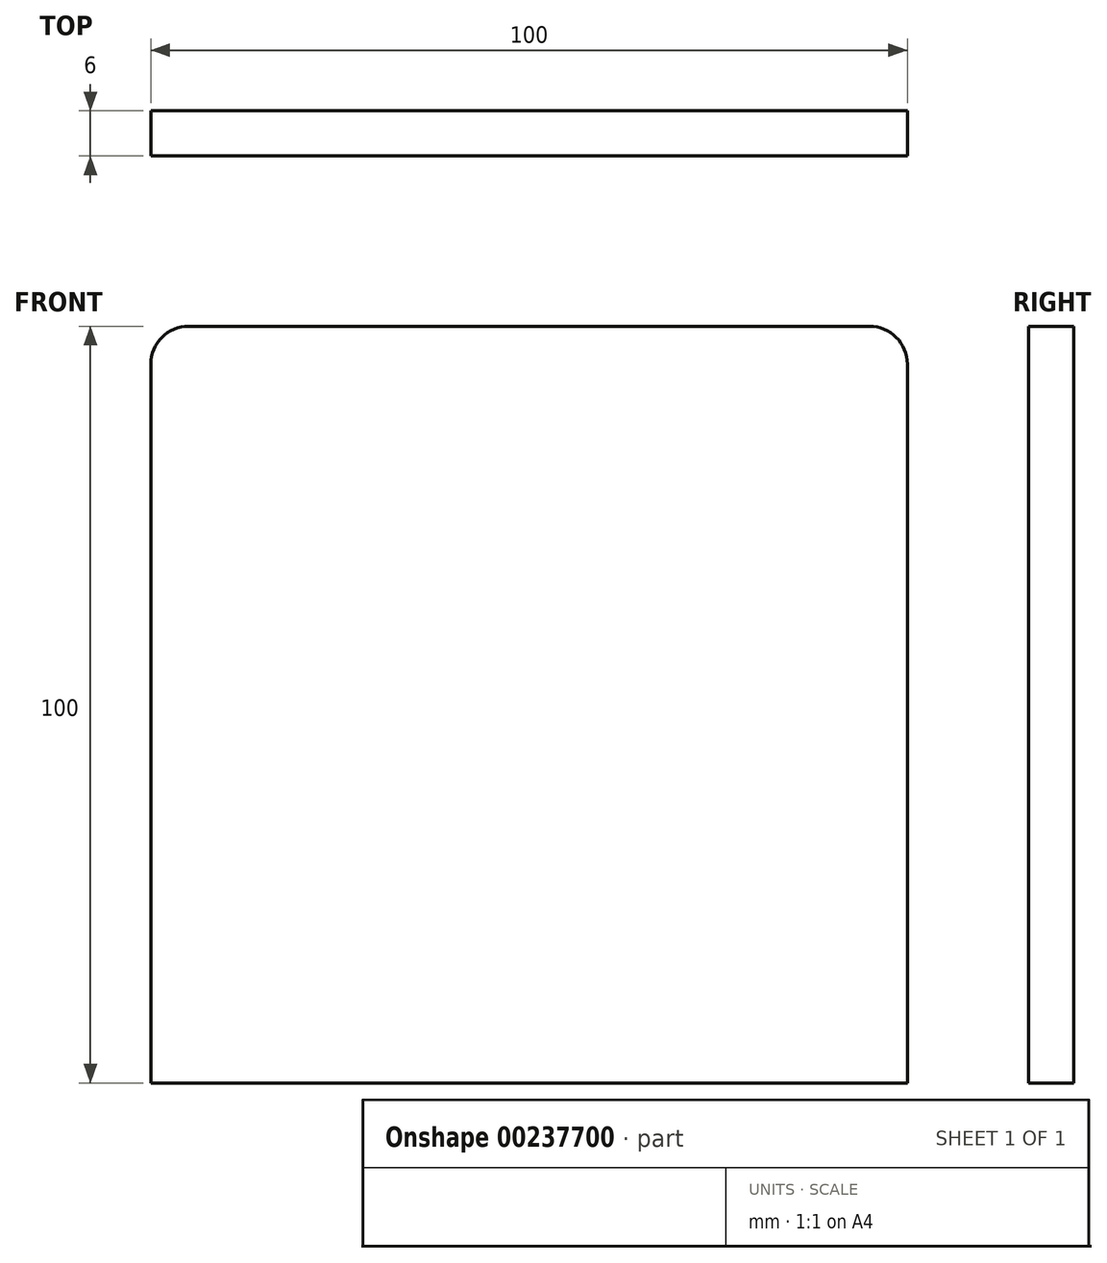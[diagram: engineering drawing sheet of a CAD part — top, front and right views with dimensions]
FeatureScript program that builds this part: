
annotation { "Feature Type Name" : "Feature", "Feature Type Description" : "" }
export const myFeature = defineFeature(function(context is Context, id is Id, definition is map)
    precondition{}
    {
        {
            var Q0;
            Q0=qCreatedBy(makeId("Front.planeOp"),FACE);
            var sketch = newSketch(context, id + "F0", { "sketchPlane" : qUnion([Q0])});
            skLineSegment(sketch, "E0.bottom", {"start": v(45, 50) * mm, "end": v(-45, 50) * mm});
            skLineSegment(sketch, "E0.top", {"start": v(50, -50) * mm, "end": v(-50, -50) * mm});
            skLineSegment(sketch, "E0.left", {"start": v(50, 45) * mm, "end": v(50, -50) * mm});
            skLineSegment(sketch, "E0.right", {"start": v(-50, 45) * mm, "end": v(-50, -50) * mm});
            skPoint(sketch, "E0.middle", {"position": v(0, 0) * mm});
            skPoint(sketch, "E1.visualSharp", {"position": v(-50, 50) * mm});
            skArc(sketch, "E1.filletArc", {"start": v(-45, 50) * mm, "mid": v(-48.54, 48.54) * mm, "end": v(-50, 45) * mm});
            skPoint(sketch, "E2.visualSharp", {"position": v(50, 50) * mm});
            skArc(sketch, "E2.filletArc", {"start": v(50, 45) * mm, "mid": v(48.54, 48.54) * mm, "end": v(45, 50) * mm});
            skLineSegment(sketch, "E3.1.0.0", {"start": v(-2, 50) * mm, "end": v(-92, 50) * mm});
            skLineSegment(sketch, "E3.direction1", {"start": v(-45, 50) * mm, "end": v(-92, 50) * mm, "construction": true});
            skPoint(sketch, "E4.oppositeSnap0", {"position": v(-50, -2.5) * mm});
            skLineSegment(sketch, "E4.left", {"start": v(-50, -1.5) * mm, "end": v(-50, -2.5) * mm});
            skLineSegment(sketch, "E4.right", {"start": v(50, -1.5) * mm, "end": v(50, -2.5) * mm});
            skSolve(sketch);
        }
        {
            var Q0;
            Q0=makeQuery(id+"F0.imprint","IMPRINT",FACE,{"disambiguationData":[TD([[makeQuery(id+"F0.imprint","IMPRINT",EDGE,{"derivedFrom":sQuery(id+"F0.wireOp",EDGE,"E0.bottom")}),1.0]])]});
            extrude(context, id + "F1", {"entities" : qUnion([Q0]), "depth" : 6 * mm});
        }
    });
